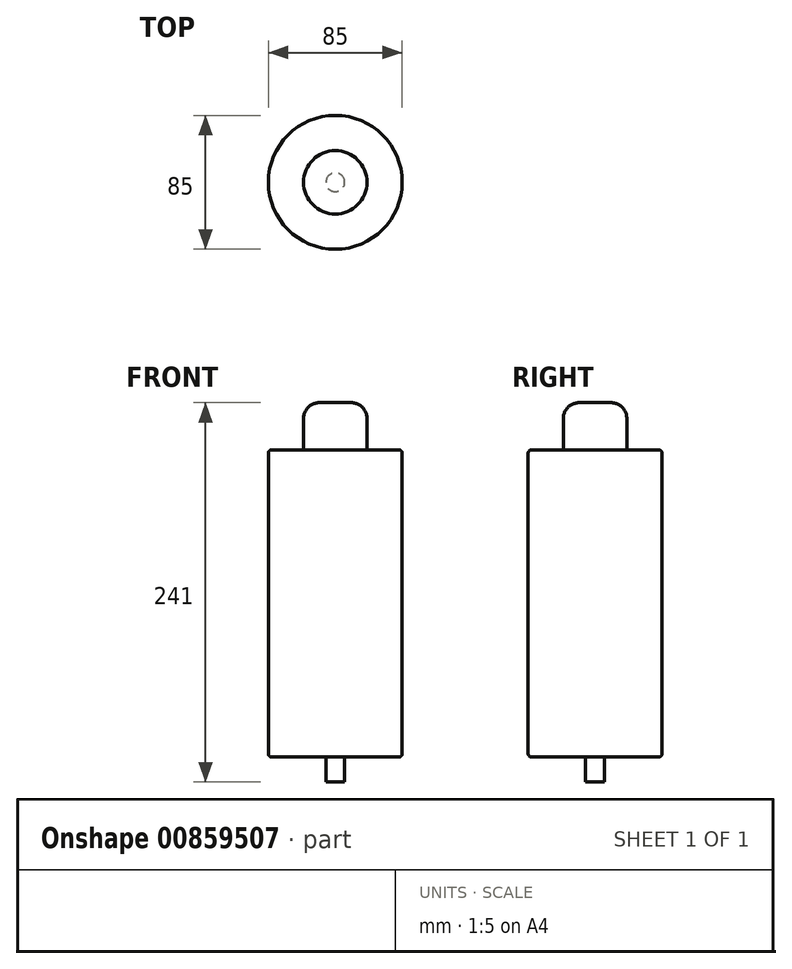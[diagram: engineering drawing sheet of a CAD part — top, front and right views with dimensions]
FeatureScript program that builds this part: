
annotation { "Feature Type Name" : "Feature", "Feature Type Description" : "" }
export const myFeature = defineFeature(function(context is Context, id is Id, definition is map)
    precondition{}
    {
        {
            var Q0;
            Q0=qCreatedBy(makeId("Top.planeOp"),FACE);
            var sketch = newSketch(context, id + "F0", { "sketchPlane" : qUnion([Q0])});
            skCircle(sketch, "E0", {"center": v(0, 0) * mm, "radius": 42.5 * mm});
            skSolve(sketch);
        }
        {
            var Q0;
            Q0=qSketchRegion(id+"F0",true);
            extrude(context, id + "F1", {"entities" : qUnion([Q0]), "depth" : 195 * mm, "offsetDistance" : 25 * mm});
        }
        {
            var Q0;
            Q0=makeQuery(id+"F1.opExtrude","CAP_FACE",FACE,{"disambiguationData":[OSD([sQuery(id+"F0.wireOp",EDGE,"E0")])],"isStart":false});
            var sketch = newSketch(context, id + "F2", { "sketchPlane" : qUnion([Q0])});
            skCircle(sketch, "E1", {"center": v(0, 0) * mm, "radius": 20.14 * mm});
            skSolve(sketch);
        }
        {
            var Q0;
            Q0=makeQuery(id+"F2.imprint","IMPRINT",FACE,{"disambiguationData":[TD([[makeQuery(id+"F2.imprint","IMPRINT",EDGE,{"derivedFrom":sQuery(id+"F2.wireOp",EDGE,"E1")}),1.0]])]});
            extrude(context, id + "F3", {"entities" : qUnion([Q0]), "operationType" : NewBodyOperationType.ADD, "depth" : 30 * mm, "offsetDistance" : 25 * mm});
        }
        {
            var Q0;
            Q0=makeQuery(id+"F3.opExtrude","CAP_EDGE",EDGE,{"disambiguationData":[OSD([sQuery(id+"F2.wireOp",EDGE,"E1")])],"isStart":false});
            fillet(context, id + "F4", {"entities" : qUnion([Q0]), "radius" : 10 * mm, "tangentPropagation" : true, "allowEdgeOverflow" : false});
        }
        {
            var Q0;
            Q0=makeQuery(id+"F1.opExtrude","CAP_FACE",FACE,{"disambiguationData":[OSD([sQuery(id+"F0.wireOp",EDGE,"E0")])],"isStart":true});
            var sketch = newSketch(context, id + "F5", { "sketchPlane" : qUnion([Q0])});
            skCircle(sketch, "E2", {"center": v(0, 0) * mm, "radius": 6 * mm});
            skSolve(sketch);
        }
        {
            var Q0;
            Q0=makeQuery(id+"F5.imprint","IMPRINT",FACE,{"disambiguationData":[TD([[makeQuery(id+"F5.imprint","IMPRINT",EDGE,{"derivedFrom":sQuery(id+"F5.wireOp",EDGE,"E2")}),1.0]])]});
            extrude(context, id + "F6", {"entities" : qUnion([Q0]), "operationType" : NewBodyOperationType.ADD, "depth" : 16 * mm, "offsetDistance" : 25 * mm});
        }
        {
            var Q0;
            Q0=makeQuery(id+"F1.opExtrude","CAP_EDGE",EDGE,{"disambiguationData":[OSD([sQuery(id+"F0.wireOp",EDGE,"E0")])],"isStart":false});
            var Q1;
            Q1=makeQuery(id+"F1.opExtrude","CAP_EDGE",EDGE,{"disambiguationData":[OSD([sQuery(id+"F0.wireOp",EDGE,"E0")])],"isStart":true});
            fillet(context, id + "F7", {"entities" : qUnion([Q0, Q1]), "radius" : 2 * mm, "tangentPropagation" : true, "allowEdgeOverflow" : false});
        }
    });
